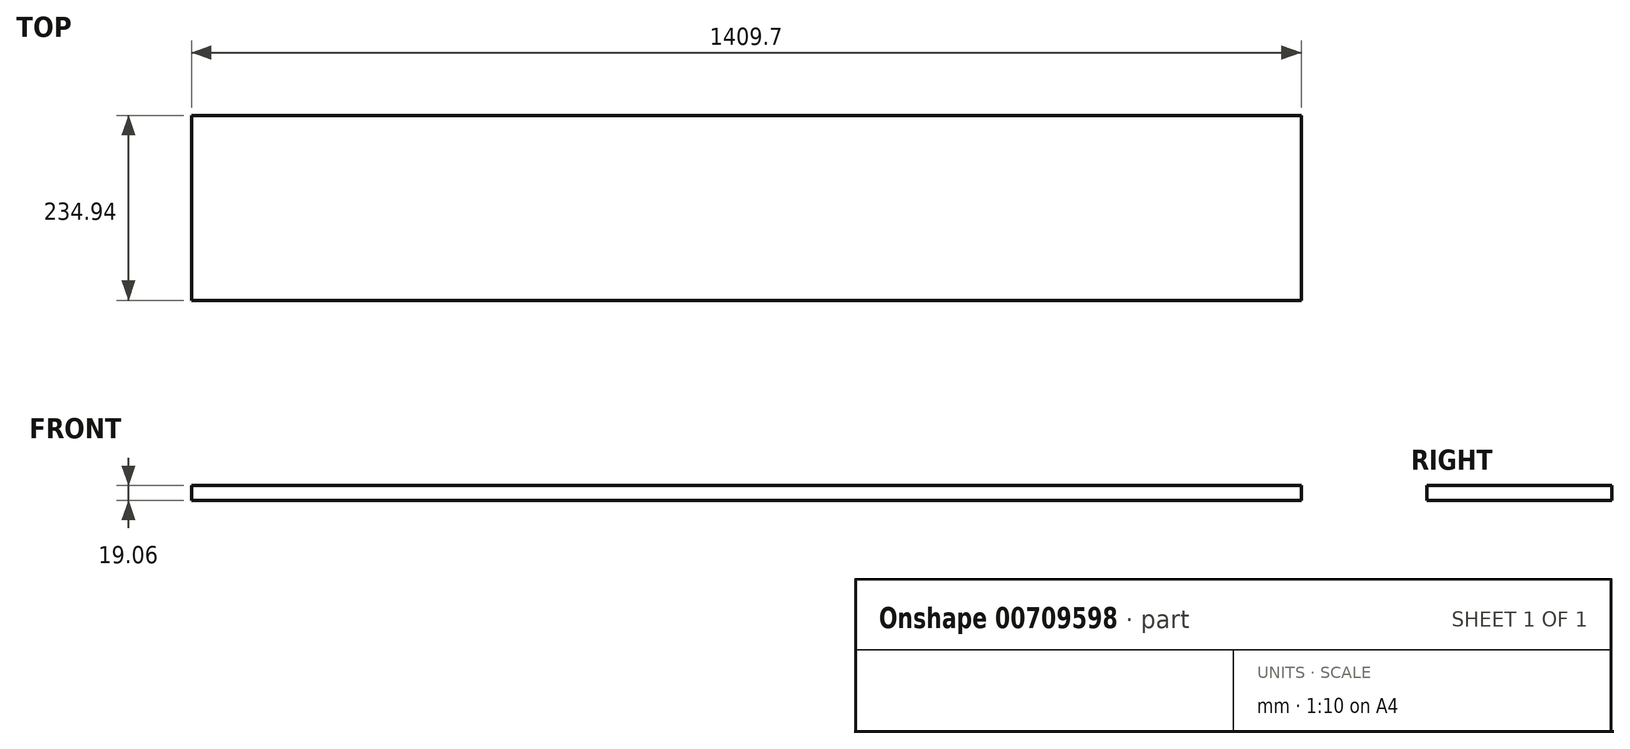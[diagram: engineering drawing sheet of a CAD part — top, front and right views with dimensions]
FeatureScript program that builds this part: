
annotation { "Feature Type Name" : "Feature", "Feature Type Description" : "" }
export const myFeature = defineFeature(function(context is Context, id is Id, definition is map)
    precondition{}
    {
        {
            var Q0;
            Q0=qCreatedBy(makeId("Top.planeOp"),FACE);
            var sketch = newSketch(context, id + "F0", { "sketchPlane" : qUnion([Q0])});
            skLineSegment(sketch, "E0.bottom", {"start": v(704.85, -117.47) * mm, "end": v(-704.85, -117.47) * mm});
            skLineSegment(sketch, "E0.top", {"start": v(704.85, 117.48) * mm, "end": v(-704.85, 117.47) * mm});
            skLineSegment(sketch, "E0.left", {"start": v(704.85, -117.47) * mm, "end": v(704.85, 117.48) * mm});
            skLineSegment(sketch, "E0.right", {"start": v(-704.85, -117.47) * mm, "end": v(-704.85, 117.48) * mm});
            skPoint(sketch, "E0.middle", {"position": v(0, 0) * mm});
            skSolve(sketch);
        }
        {
            var Q0;
            Q0=makeQuery(id+"F0.imprint","IMPRINT",FACE,{"disambiguationData":[TD([[makeQuery(id+"F0.imprint","IMPRINT",EDGE,{"derivedFrom":sQuery(id+"F0.wireOp",EDGE,"E0.bottom")}),-1.0]])]});
            extrude(context, id + "F1", {"entities" : qUnion([Q0]), "endBound" : BoundingType.SYMMETRIC, "depth" : 19.05 * mm, "offsetDistance" : 25.4 * mm});
        }
    });
